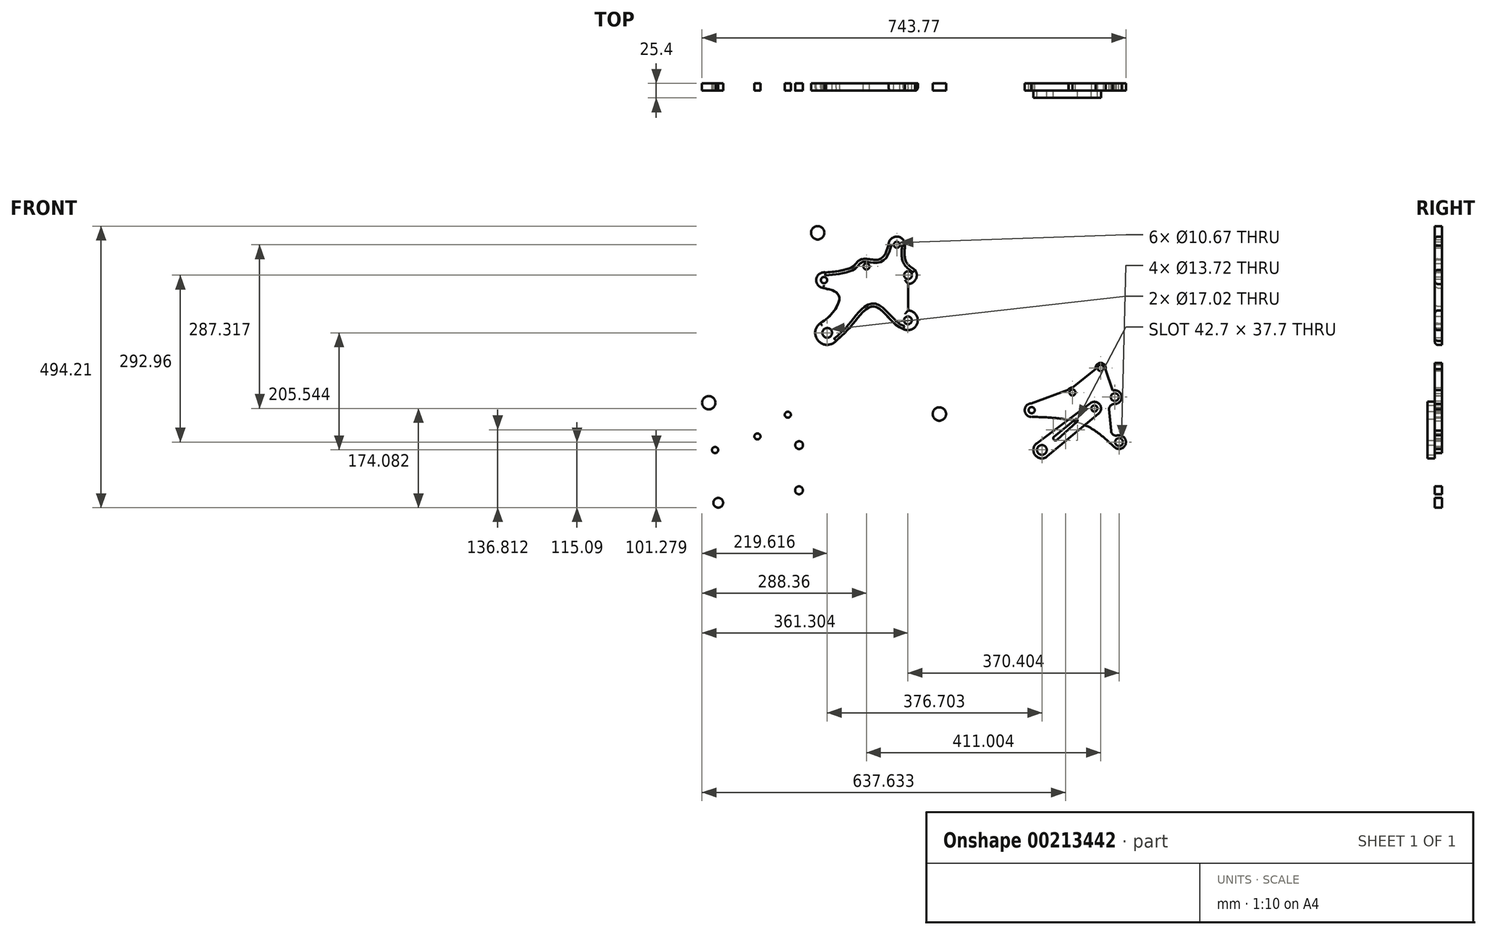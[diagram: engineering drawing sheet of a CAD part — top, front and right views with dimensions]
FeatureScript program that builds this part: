
annotation { "Feature Type Name" : "Feature", "Feature Type Description" : "" }
export const myFeature = defineFeature(function(context is Context, id is Id, definition is map)
    precondition{}
    {
        {
            var Q0;
            Q0=qCreatedBy(makeId("Front.planeOp"),FACE);
            var sketch = newSketch(context, id + "F0", { "sketchPlane" : qUnion([Q0])});
            skCircle(sketch, "E0", {"center": v(-75.71, 40.93) * mm, "radius": 6.86 * mm});
            skCircle(sketch, "E1", {"center": v(-75.87, -38.31) * mm, "radius": 6.86 * mm});
            skCircle(sketch, "E2", {"center": v(-217.56, -60.3) * mm, "radius": 8.5 * mm});
            skCircle(sketch, "E3", {"center": v(-223.16, 32.25) * mm, "radius": 5.46 * mm});
            skCircle(sketch, "E4", {"center": v(-148.82, 56.19) * mm, "radius": 5.33 * mm});
            skCircle(sketch, "E5", {"center": v(-95.5, 94.28) * mm, "radius": 5.33 * mm});
            skCircle(sketch, "E6", {"center": v(-234.25, 115.32) * mm, "radius": 11.77 * mm});
            skCircle(sketch, "E7", {"center": v(478.2, 125.18) * mm, "radius": 6.86 * mm});
            skCircle(sketch, "E8", {"center": v(485.7, 46.3) * mm, "radius": 6.86 * mm});
            skCircle(sketch, "E9", {"center": v(332.28, 102.29) * mm, "radius": 5.46 * mm});
            skCircle(sketch, "E10", {"center": v(403.96, 133.3) * mm, "radius": 5.33 * mm});
            skCircle(sketch, "E11", {"center": v(453.35, 176.37) * mm, "radius": 5.33 * mm});
            skCircle(sketch, "E12", {"center": v(170.43, 95.58) * mm, "radius": 11.77 * mm});
            skCircle(sketch, "E13", {"center": v(115.45, 339.25) * mm, "radius": 6.86 * mm});
            skCircle(sketch, "E14", {"center": v(115.3, 260) * mm, "radius": 6.86 * mm});
            skCircle(sketch, "E15", {"center": v(-26.4, 238.02) * mm, "radius": 8.5 * mm});
            skCircle(sketch, "E16", {"center": v(-32, 330.56) * mm, "radius": 5.46 * mm});
            skCircle(sketch, "E17", {"center": v(42.35, 354.5) * mm, "radius": 5.33 * mm});
            skCircle(sketch, "E18", {"center": v(95.67, 392.6) * mm, "radius": 5.33 * mm});
            skCircle(sketch, "E19", {"center": v(-43.08, 413.64) * mm, "radius": 11.77 * mm});
            skArc(sketch, "E20", {"start": v(109.98, 390.97) * mm, "mid": v(96.56, 406.97) * mm, "end": v(81.27, 392.75) * mm});
            skArc(sketch, "E21", {"start": v(115.45, 323.88) * mm, "mid": v(129.15, 332.28) * mm, "end": v(127.87, 348.3) * mm});
            skArc(sketch, "E22", {"start": v(106.9, 244.97) * mm, "mid": v(131.94, 255.59) * mm, "end": v(115.45, 277.22) * mm});
            skArc(sketch, "E23", {"start": v(-38.32, 255.3) * mm, "mid": v(-42.07, 224.06) * mm, "end": v(-10.6, 224.19) * mm});
            skArc(sketch, "E24", {"start": v(-29.31, 344) * mm, "mid": v(-45.56, 332.48) * mm, "end": v(-33.13, 316.9) * mm});
            skLineSegment(sketch, "E25", {"start": v(87.84, 404.68) * mm, "end": v(85.25, 402.54) * mm});
            skLineSegment(sketch, "E26", {"start": v(108.19, 399.72) * mm, "end": v(109.75, 395.66) * mm});
            skLineSegment(sketch, "E27", {"start": v(115.45, 354.65) * mm, "end": v(115.45, 354.62) * mm});
            skLineSegment(sketch, "E28", {"start": v(115.45, 323.88) * mm, "end": v(115.45, 277.22) * mm});
            skFitSpline(sketch, "E29", {"points": [v(-33.13, 316.9) * mm, v(-16.27, 312.25) * mm, v(-5.06, 298.43) * mm, v(-38.32, 255.3) * mm], "startDerivative": vector(89.78, -29.63) * mm, "endDerivative": vector(-99.64, -49.75) * mm});
            skFitSpline(sketch, "E30", {"points": [v(-10.6, 224.19) * mm, v(19.98, 255.3) * mm, v(45.77, 282.07) * mm, v(65.88, 280.02) * mm, v(106.9, 244.97) * mm], "startDerivative": vector(227.4, 204.66) * mm, "endDerivative": vector(158.06, -50.91) * mm});
            skFitSpline(sketch, "E31", {"points": [v(-29.31, 344) * mm, v(15.02, 352.2) * mm, v(22.37, 357.78) * mm, v(34.23, 367.4) * mm, v(60.77, 366.3) * mm, v(75.33, 376.33) * mm, v(85.25, 402.54) * mm], "startDerivative": vector(222.43, 12.67) * mm, "endDerivative": vector(72.08, 134.25) * mm});
            skFitSpline(sketch, "E32", {"points": [v(110.07, 392.2) * mm, v(109.65, 371.57) * mm, v(114.1, 359.5) * mm, v(127.87, 348.3) * mm], "startDerivative": vector(-4.24, -59.71) * mm, "endDerivative": vector(46.46, -31.21) * mm});
            skPoint(sketch, "E33.start.orphan", {"position": v(41.54, 366.3) * mm});
            skArc(sketch, "E34", {"start": v(404.13, 142.19) * mm, "mid": v(399.9, 141.2) * mm, "end": v(396.64, 138.34) * mm});
            skArc(sketch, "E35", {"start": v(462.06, 174.57) * mm, "mid": v(453.13, 185.26) * mm, "end": v(444.75, 174.13) * mm});
            skArc(sketch, "E36", {"start": v(477.6, 113.13) * mm, "mid": v(490.16, 126.73) * mm, "end": v(474.54, 136.68) * mm});
            skArc(sketch, "E37", {"start": v(331.67, 114.33) * mm, "mid": v(320.3, 100.77) * mm, "end": v(334.68, 90.46) * mm});
            skFitSpline(sketch, "E38", {"points": [v(476.42, 38.58) * mm, v(434.34, 71.87) * mm, v(384.25, 87.3) * mm, v(334.68, 90.46) * mm], "startDerivative": vector(-117.52, 109.73) * mm, "endDerivative": vector(-151, 3.56) * mm});
            skArc(sketch, "E39", {"start": v(477.6, 113.13) * mm, "mid": v(470.16, 109.7) * mm, "end": v(468.31, 101.73) * mm});
            skArc(sketch, "E40", {"start": v(471.65, 66.68) * mm, "mid": v(474.52, 59.93) * mm, "end": v(481.47, 57.6) * mm});
            skLineSegment(sketch, "E41.trimOffspring", {"start": v(471.65, 66.68) * mm, "end": v(468.08, 104.16) * mm});
            skArc(sketch, "E42.trimOffspring", {"start": v(476.42, 38.58) * mm, "mid": v(497.36, 43.19) * mm, "end": v(481.47, 57.6) * mm});
            skLineSegment(sketch, "E43", {"start": v(474.54, 136.68) * mm, "end": v(462.06, 174.57) * mm});
            skLineSegment(sketch, "E44", {"start": v(444.75, 174.13) * mm, "end": v(404.13, 142.19) * mm});
            skLineSegment(sketch, "E45", {"start": v(396.64, 138.34) * mm, "end": v(331.67, 114.33) * mm});
            skSolve(sketch);
        }
        {
            var Q0;
            Q0 = qSketchRegion(id + "F0", true);
            extrude(context, id + "F1", {"entities" : qUnion([Q0]), "depth" : 12.7 * mm});
        }
        {
            var Q0;
            Q0=makeQuery(id+"F1.opExtrude","CAP_EDGE",EDGE,{"disambiguationData":[OSD([sQuery(id+"F0.wireOp",EDGE,"E30")])],"isStart":false});
            var Q1;
            Q1=makeQuery(id+"F1.opExtrude","CAP_EDGE",EDGE,{"disambiguationData":[OSD([sQuery(id+"F0.wireOp",EDGE,"E23")])],"isStart":false});
            var Q2;
            Q2=makeQuery(id+"F1.opExtrude","CAP_EDGE",EDGE,{"disambiguationData":[OSD([sQuery(id+"F0.wireOp",EDGE,"E29")])],"isStart":false});
            var Q3;
            Q3=makeQuery(id+"F1.opExtrude","CAP_EDGE",EDGE,{"disambiguationData":[OSD([sQuery(id+"F0.wireOp",EDGE,"E24")])],"isStart":false});
            var Q4;
            Q4=makeQuery(id+"F1.opExtrude","CAP_EDGE",EDGE,{"disambiguationData":[OSD([sQuery(id+"F0.wireOp",EDGE,"E31")])],"isStart":false});
            var Q5;
            Q5=makeQuery(id+"F1.opExtrude","CAP_EDGE",EDGE,{"disambiguationData":[OSD([sQuery(id+"F0.wireOp",EDGE,"E28")])],"isStart":false});
            var Q6;
            Q6=makeQuery(id+"F1.opExtrude","CAP_EDGE",EDGE,{"disambiguationData":[OSD([sQuery(id+"F0.wireOp",EDGE,"E22")])],"isStart":false});
            var Q7;
            Q7=makeQuery(id+"F1.opExtrude","CAP_EDGE",EDGE,{"disambiguationData":[OSD([sQuery(id+"F0.wireOp",EDGE,"E32")])],"isStart":false});
            var Q8;
            Q8=makeQuery(id+"F1.opExtrude","CAP_EDGE",EDGE,{"disambiguationData":[OSD([sQuery(id+"F0.wireOp",EDGE,"E21")])],"isStart":false});
            var Q9;
            Q9=makeQuery(id+"F1.opExtrude","CAP_EDGE",EDGE,{"disambiguationData":[OSD([sQuery(id+"F0.wireOp",EDGE,"E20")])],"isStart":false});
            fillet(context, id + "F2", {"entities" : qUnion([Q0, Q1, Q2, Q3, Q4, Q5, Q6, Q7, Q8, Q9]), "radius" : 5.08 * mm, "tangentPropagation" : true, "allowEdgeOverflow" : false});
        }
        {
            var Q0;
            Q0=makeQuery(id+"F1.opExtrude","CAP_FACE",FACE,{"disambiguationData":[OSD([sQuery(id+"F0.wireOp",EDGE,"E7"),sQuery(id+"F0.wireOp",EDGE,"E8"),sQuery(id+"F0.wireOp",EDGE,"851a4d25-ab60-4b78-9207-1267376989fa"),sQuery(id+"F0.wireOp",EDGE,"E9"),sQuery(id+"F0.wireOp",EDGE,"E10"),sQuery(id+"F0.wireOp",EDGE,"E11"),sQuery(id+"F0.wireOp",EDGE,"E34"),sQuery(id+"F0.wireOp",EDGE,"E35"),sQuery(id+"F0.wireOp",EDGE,"E36"),sQuery(id+"F0.wireOp",EDGE,"E37"),sQuery(id+"F0.wireOp",EDGE,"f1oDUusj-p2Wh-kuyW-nnhu-89Pm8JZUcBxC"),sQuery(id+"F0.wireOp",EDGE,"E38"),sQuery(id+"F0.wireOp",EDGE,"E39"),sQuery(id+"F0.wireOp",EDGE,"E40"),sQuery(id+"F0.wireOp",EDGE,"E41.trimOffspring"),sQuery(id+"F0.wireOp",EDGE,"E42.trimOffspring"),sQuery(id+"F0.wireOp",EDGE,"10928a58-aef1-4146-bc66-b8e2b748299b"),sQuery(id+"F0.wireOp",EDGE,"b3645b89-29fa-433f-939d-fef8fdfaf921"),sQuery(id+"F0.wireOp",EDGE,"E43"),sQuery(id+"F0.wireOp",EDGE,"E44"),sQuery(id+"F0.wireOp",EDGE,"E45")])],"isStart":false});
            var sketch = newSketch(context, id + "F3", { "sketchPlane" : qUnion([Q0])});
            skCircle(sketch, "E46", {"center": v(442.4, 105.28) * mm, "radius": 5.33 * mm});
            skCircle(sketch, "E47", {"center": v(350.3, 32.48) * mm, "radius": 8.5 * mm});
            skArc(sketch, "E48", {"start": v(341.41, 44.38) * mm, "mid": v(338.65, 23.26) * mm, "end": v(359.84, 21.08) * mm});
            skArc(sketch, "E49", {"start": v(449.89, 96.32) * mm, "mid": v(451.56, 112.53) * mm, "end": v(435.4, 114.64) * mm});
            skLineSegment(sketch, "E50", {"start": v(341.41, 44.38) * mm, "end": v(435.4, 114.64) * mm});
            skLineSegment(sketch, "E51", {"start": v(449.89, 96.32) * mm, "end": v(359.84, 21.08) * mm});
            skArc(sketch, "E52", {"start": v(371.66, 55.92) * mm, "mid": v(371.18, 50.48) * mm, "end": v(376.63, 50.15) * mm});
            skArc(sketch, "E53", {"start": v(412.15, 82.45) * mm, "mid": v(412.36, 85.99) * mm, "end": v(408.83, 86.3) * mm});
            skLineSegment(sketch, "E54", {"start": v(371.66, 55.92) * mm, "end": v(408.83, 86.3) * mm});
            skLineSegment(sketch, "E55", {"start": v(376.63, 50.15) * mm, "end": v(412.15, 82.45) * mm});
            skSolve(sketch);
        }
        {
            var Q0;
            Q0 = qSketchRegion(id + "F3", true);
            extrude(context, id + "F4", {"entities" : qUnion([Q0]), "depth" : 12.7 * mm});
        }
        {
            var Q0;
            Q0=makeQuery(id+"F1.opExtrude","CAP_FACE",FACE,{"disambiguationData":[OSD([sQuery(id+"F0.wireOp",EDGE,"E7"),sQuery(id+"F0.wireOp",EDGE,"E8"),sQuery(id+"F0.wireOp",EDGE,"851a4d25-ab60-4b78-9207-1267376989fa"),sQuery(id+"F0.wireOp",EDGE,"E9"),sQuery(id+"F0.wireOp",EDGE,"E10"),sQuery(id+"F0.wireOp",EDGE,"E11"),sQuery(id+"F0.wireOp",EDGE,"E34"),sQuery(id+"F0.wireOp",EDGE,"E35"),sQuery(id+"F0.wireOp",EDGE,"E36"),sQuery(id+"F0.wireOp",EDGE,"E37"),sQuery(id+"F0.wireOp",EDGE,"f1oDUusj-p2Wh-kuyW-nnhu-89Pm8JZUcBxC"),sQuery(id+"F0.wireOp",EDGE,"E38"),sQuery(id+"F0.wireOp",EDGE,"E39"),sQuery(id+"F0.wireOp",EDGE,"E40"),sQuery(id+"F0.wireOp",EDGE,"E41.trimOffspring"),sQuery(id+"F0.wireOp",EDGE,"E42.trimOffspring"),sQuery(id+"F0.wireOp",EDGE,"10928a58-aef1-4146-bc66-b8e2b748299b"),sQuery(id+"F0.wireOp",EDGE,"b3645b89-29fa-433f-939d-fef8fdfaf921"),sQuery(id+"F0.wireOp",EDGE,"E43"),sQuery(id+"F0.wireOp",EDGE,"E44"),sQuery(id+"F0.wireOp",EDGE,"E45")])],"isStart":false});
            var sketch = newSketch(context, id + "F5", { "sketchPlane" : qUnion([Q0])});
            skCircle(sketch, "E56", {"center": v(442.4, 105.28) * mm, "radius": 5.33 * mm});
            skSolve(sketch);
        }
        {
            var Q0;
            Q0 = qSketchRegion(id + "F5", true);
            extrude(context, id + "F6", {"entities" : qUnion([Q0]), "operationType" : NewBodyOperationType.REMOVE, "oppositeDirection" : true, "depth" : 25.4 * mm});
        }
    });
